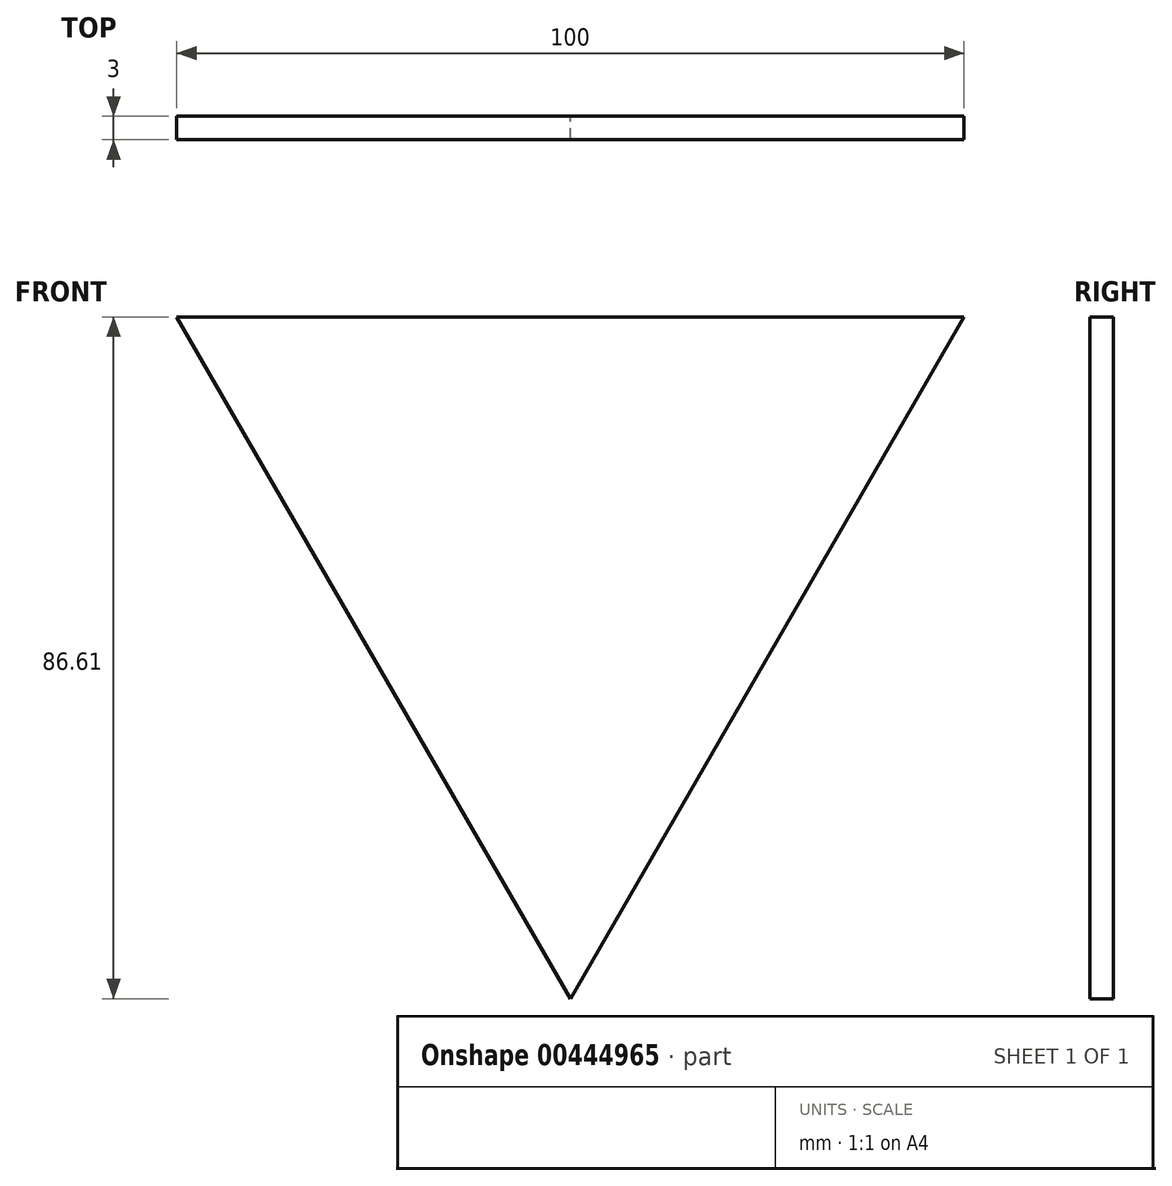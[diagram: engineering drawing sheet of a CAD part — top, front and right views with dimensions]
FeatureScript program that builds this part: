
annotation { "Feature Type Name" : "Feature", "Feature Type Description" : "" }
export const myFeature = defineFeature(function(context is Context, id is Id, definition is map)
    precondition{}
    {
        {
            var Q0;
            Q0=qCreatedBy(makeId("Front.planeOp"),FACE);
            var sketch = newSketch(context, id + "F0", { "sketchPlane" : qUnion([Q0])});
            skCircle(sketch, "E0.cCircle", {"center": v(0, 0) * mm, "radius": 28.87 * mm, "construction": true});
            skLineSegment(sketch, "E0.0", {"start": v(-50, 28.87) * mm, "end": v(50, 28.87) * mm});
            skLineSegment(sketch, "E0.1", {"start": v(50, 28.87) * mm, "end": v(0, -57.74) * mm});
            skLineSegment(sketch, "E0.2", {"start": v(0, -57.74) * mm, "end": v(-50, 28.87) * mm});
            skPoint(sketch, "E0.0.midPoint", {"position": v(0, 28.87) * mm});
            skSolve(sketch);
        }
        {
            var Q0;
            Q0 = qSketchRegion(id + "F0", true);
            extrude(context, id + "F1", {"entities" : qUnion([Q0]), "depth" : 3 * mm});
        }
    });
